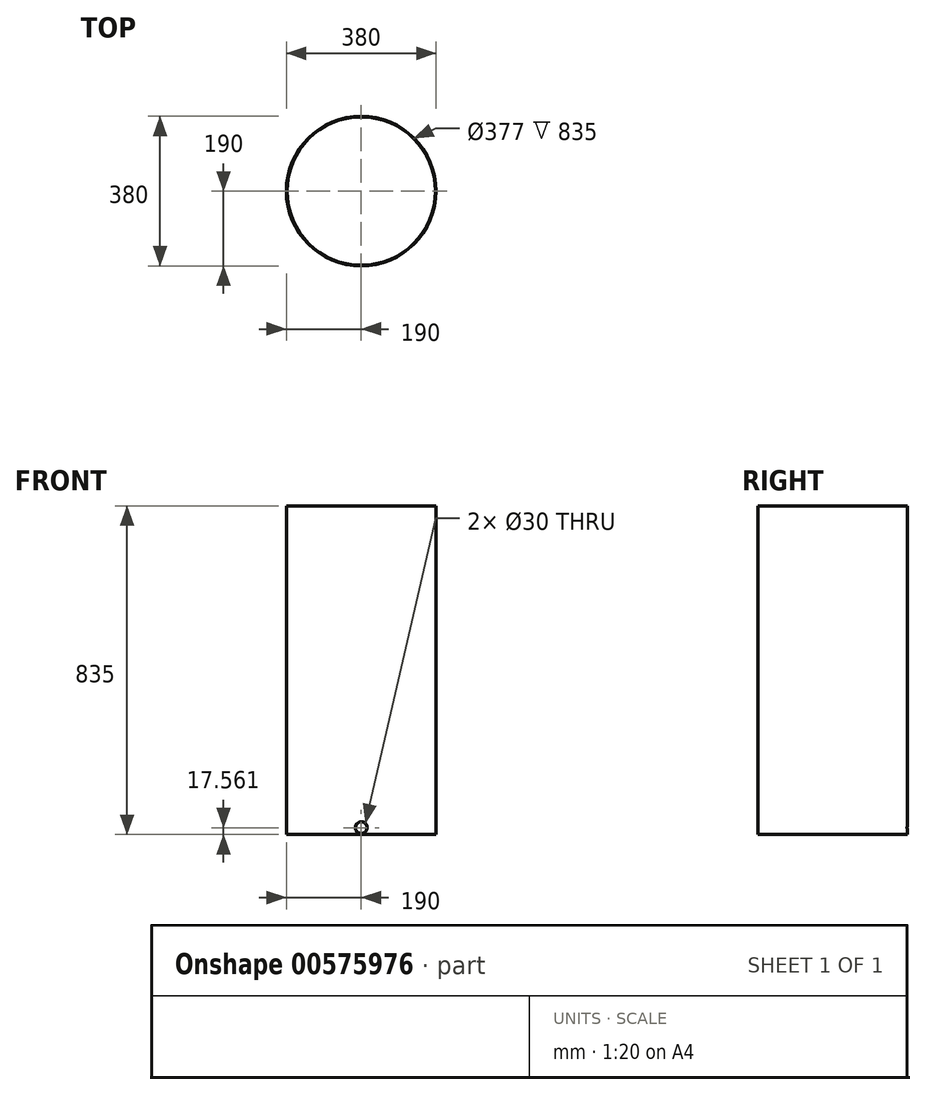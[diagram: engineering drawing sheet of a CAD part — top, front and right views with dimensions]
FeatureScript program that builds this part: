
annotation { "Feature Type Name" : "Feature", "Feature Type Description" : "" }
export const myFeature = defineFeature(function(context is Context, id is Id, definition is map)
    precondition{}
    {
        {
            var Q0;
            Q0=qCreatedBy(makeId("Right.planeOp"),FACE);
            var sketch = newSketch(context, id + "F0", { "sketchPlane" : qUnion([Q0])});
            skLineSegment(sketch, "E0", {"start": v(0, 172.18) * mm, "end": v(0, -191.69) * mm, "construction": true});
            skLineSegment(sketch, "E1.bottom", {"start": v(-190, 835) * mm, "end": v(-188.5, 835) * mm});
            skLineSegment(sketch, "E1.top", {"start": v(-190, 0) * mm, "end": v(-188.5, 0) * mm});
            skLineSegment(sketch, "E1.left", {"start": v(-190, 835) * mm, "end": v(-190, 0) * mm});
            skLineSegment(sketch, "E1.right", {"start": v(-188.5, 835) * mm, "end": v(-188.5, 0) * mm});
            skSolve(sketch);
        }
        {
            var Q0;
            Q0=makeQuery(id+"F0.imprint","IMPRINT",FACE,{"disambiguationData":[TD([[makeQuery(id+"F0.imprint","IMPRINT",EDGE,{"derivedFrom":sQuery(id+"F0.wireOp",EDGE,"E1.bottom")}),-1.0]])]});
            var Q1;
            Q1=sQuery(id+"F0.wireOp",EDGE,"vArjbrbD-3ZTj-1tds-upoA-ewURFE757hO0");
            var Q2;
            Q2=sQuery(id+"F0.wireOp",EDGE,"E0");
            revolve(context, id + "F1", {"entities" : qUnion([Q0]), "surfaceEntities" : qUnion([Q1]), "axis" : qUnion([Q2]), "revolveType" : RevolveType.FULL, "surfaceOperationType" : NewSurfaceOperationType.NEW});
        }
        {
            var Q0;
            Q0=qCreatedBy(makeId("Front.planeOp"),FACE);
            var sketch = newSketch(context, id + "F2", { "sketchPlane" : qUnion([Q0])});
            skCircle(sketch, "E2", {"center": v(0, 17.56) * mm, "radius": 15 * mm});
            skSolve(sketch);
        }
        {
            var Q0;
            Q0 = qSketchRegion(id + "F2", true);
            extrude(context, id + "F3", {"entities" : qUnion([Q0]), "operationType" : NewBodyOperationType.REMOVE, "endBound" : BoundingType.THROUGH_ALL, "depth" : 257 * mm, "offsetDistance" : 25 * mm, "hasSecondDirection" : true, "secondDirectionBound" : SecondDirectionBoundingType.THROUGH_ALL, "secondDirectionOppositeDirection" : true, "secondDirectionDepth" : 241 * mm});
        }
    });
